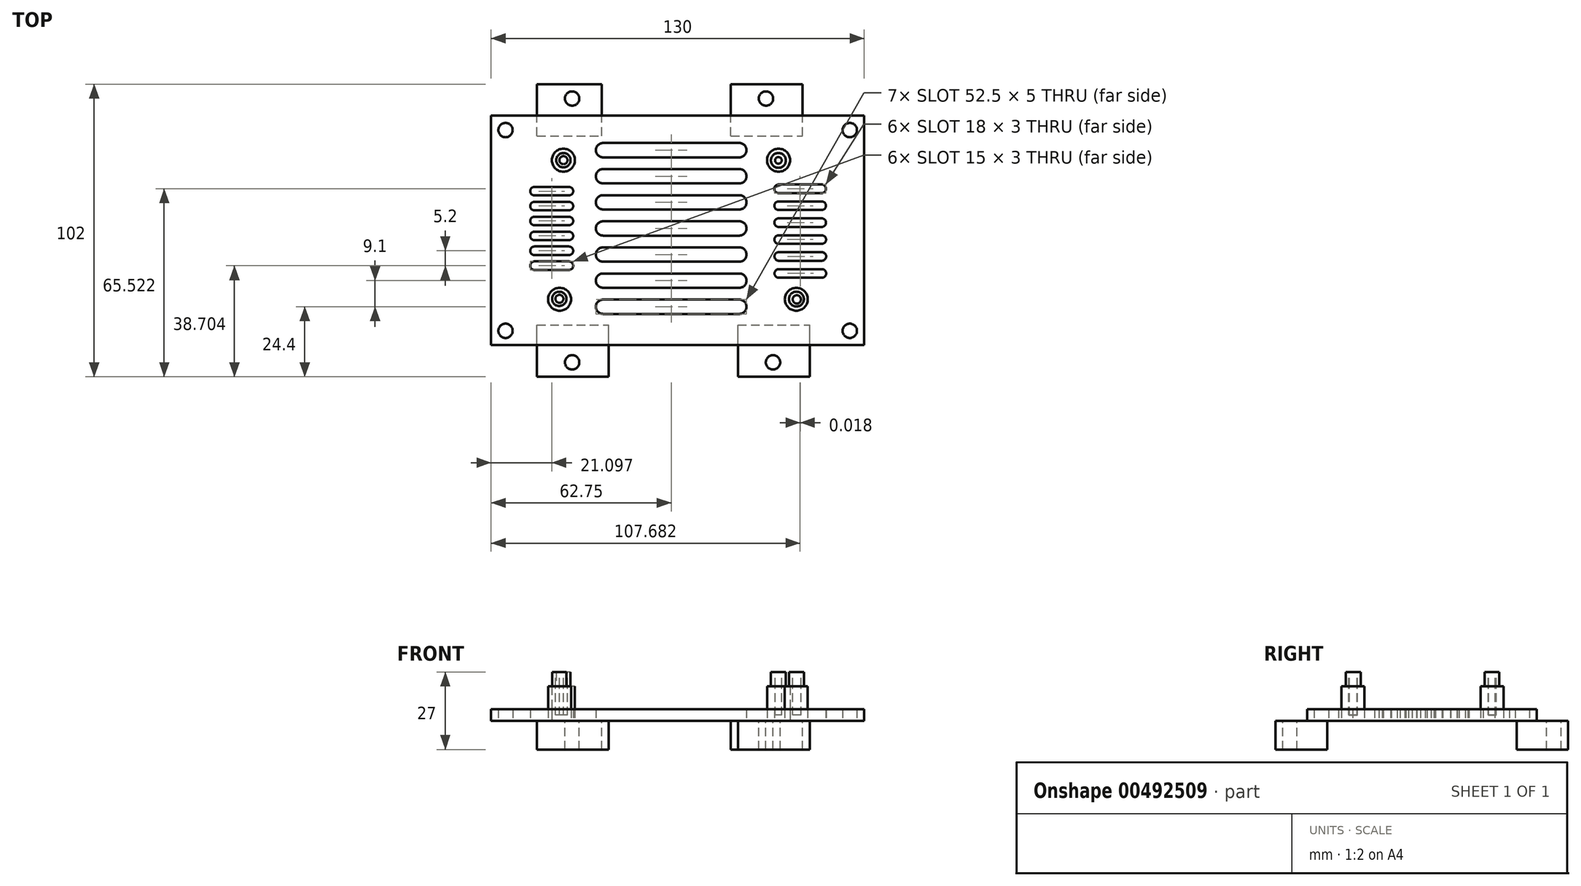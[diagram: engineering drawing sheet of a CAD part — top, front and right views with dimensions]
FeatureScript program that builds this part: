
annotation { "Feature Type Name" : "Feature", "Feature Type Description" : "" }
export const myFeature = defineFeature(function(context is Context, id is Id, definition is map)
    precondition{}
    {
        {
            var Q0;
            Q0=qCreatedBy(makeId("Top.planeOp"),FACE);
            var sketch = newSketch(context, id + "F0", { "sketchPlane" : qUnion([Q0])});
            skLineSegment(sketch, "E0.bottom", {"start": v(0, 0) * mm, "end": v(130, 0) * mm});
            skLineSegment(sketch, "E0.top", {"start": v(0, 80) * mm, "end": v(130, 80) * mm});
            skLineSegment(sketch, "E0.left", {"start": v(0, 0) * mm, "end": v(0, 80) * mm});
            skLineSegment(sketch, "E0.right", {"start": v(130, 0) * mm, "end": v(130, 80) * mm});
            skCircle(sketch, "E1", {"center": v(25.18, 64.5) * mm, "radius": 4 * mm});
            skCircle(sketch, "E2", {"center": v(23.85, 16) * mm, "radius": 4 * mm});
            skCircle(sketch, "E3", {"center": v(100.18, 64.5) * mm, "radius": 4 * mm});
            skCircle(sketch, "E4", {"center": v(106.35, 16) * mm, "radius": 4 * mm});
            skCircle(sketch, "E5", {"center": v(5, 75) * mm, "radius": 2.5 * mm});
            skCircle(sketch, "E6", {"center": v(5, 5) * mm, "radius": 2.5 * mm});
            skCircle(sketch, "E7", {"center": v(125, 75) * mm, "radius": 2.5 * mm});
            skCircle(sketch, "E8", {"center": v(125, 5) * mm, "radius": 2.5 * mm});
            skLineSegment(sketch, "E9.bottom", {"start": v(39, 70.5) * mm, "end": v(86.5, 70.5) * mm});
            skLineSegment(sketch, "E9.top", {"start": v(39, 65.5) * mm, "end": v(86.5, 65.5) * mm});
            skLineSegment(sketch, "E9.left", {"start": v(36.5, 68) * mm, "end": v(36.5, 68) * mm});
            skLineSegment(sketch, "E9.right", {"start": v(89, 68) * mm, "end": v(89, 68) * mm});
            skPoint(sketch, "E10.visualSharp", {"position": v(36.5, 70.5) * mm});
            skArc(sketch, "E10.filletArc", {"start": v(39, 70.5) * mm, "mid": v(37.23, 69.77) * mm, "end": v(36.5, 68) * mm});
            skPoint(sketch, "E11.visualSharp", {"position": v(36.5, 65.5) * mm});
            skArc(sketch, "E11.filletArc", {"start": v(36.5, 68) * mm, "mid": v(37.23, 66.23) * mm, "end": v(39, 65.5) * mm});
            skPoint(sketch, "E12.visualSharp", {"position": v(89, 70.5) * mm});
            skArc(sketch, "E12.filletArc", {"start": v(89, 68) * mm, "mid": v(88.27, 69.77) * mm, "end": v(86.5, 70.5) * mm});
            skPoint(sketch, "E13.visualSharp", {"position": v(89, 65.5) * mm});
            skArc(sketch, "E13.filletArc", {"start": v(86.5, 65.5) * mm, "mid": v(88.27, 66.23) * mm, "end": v(89, 68) * mm});
            skLineSegment(sketch, "E14.1.0.0", {"start": v(39, 56.4) * mm, "end": v(86.5, 56.4) * mm});
            skLineSegment(sketch, "E14.1.0.1", {"start": v(39, 61.4) * mm, "end": v(86.5, 61.4) * mm});
            skPoint(sketch, "E14.1.0.2", {"position": v(89, 56.4) * mm});
            skPoint(sketch, "E14.1.0.3", {"position": v(89, 61.4) * mm});
            skArc(sketch, "E14.1.0.4", {"start": v(39, 61.4) * mm, "mid": v(37.23, 60.67) * mm, "end": v(36.5, 58.9) * mm});
            skArc(sketch, "E14.1.0.5", {"start": v(86.5, 56.4) * mm, "mid": v(88.27, 57.13) * mm, "end": v(89, 58.9) * mm});
            skArc(sketch, "E14.1.0.6", {"start": v(36.5, 58.9) * mm, "mid": v(37.23, 57.13) * mm, "end": v(39, 56.4) * mm});
            skArc(sketch, "E14.1.0.7", {"start": v(89, 58.9) * mm, "mid": v(88.27, 60.67) * mm, "end": v(86.5, 61.4) * mm});
            skLineSegment(sketch, "E14.2.0.0", {"start": v(39, 47.3) * mm, "end": v(86.5, 47.3) * mm});
            skLineSegment(sketch, "E14.2.0.1", {"start": v(39, 52.3) * mm, "end": v(86.5, 52.3) * mm});
            skPoint(sketch, "E14.2.0.2", {"position": v(89, 47.3) * mm});
            skPoint(sketch, "E14.2.0.3", {"position": v(89, 52.3) * mm});
            skArc(sketch, "E14.2.0.4", {"start": v(39, 52.3) * mm, "mid": v(37.23, 51.57) * mm, "end": v(36.5, 49.8) * mm});
            skArc(sketch, "E14.2.0.5", {"start": v(86.5, 47.3) * mm, "mid": v(88.27, 48.03) * mm, "end": v(89, 49.8) * mm});
            skArc(sketch, "E14.2.0.6", {"start": v(36.5, 49.8) * mm, "mid": v(37.23, 48.03) * mm, "end": v(39, 47.3) * mm});
            skArc(sketch, "E14.2.0.7", {"start": v(89, 49.8) * mm, "mid": v(88.27, 51.57) * mm, "end": v(86.5, 52.3) * mm});
            skLineSegment(sketch, "E14.3.0.0", {"start": v(39, 38.2) * mm, "end": v(86.5, 38.2) * mm});
            skLineSegment(sketch, "E14.3.0.1", {"start": v(39, 43.2) * mm, "end": v(86.5, 43.2) * mm});
            skPoint(sketch, "E14.3.0.2", {"position": v(89, 38.2) * mm});
            skPoint(sketch, "E14.3.0.3", {"position": v(89, 43.2) * mm});
            skArc(sketch, "E14.3.0.4", {"start": v(39, 43.2) * mm, "mid": v(37.23, 42.47) * mm, "end": v(36.5, 40.7) * mm});
            skArc(sketch, "E14.3.0.5", {"start": v(86.5, 38.2) * mm, "mid": v(88.27, 38.93) * mm, "end": v(89, 40.7) * mm});
            skArc(sketch, "E14.3.0.6", {"start": v(36.5, 40.7) * mm, "mid": v(37.23, 38.93) * mm, "end": v(39, 38.2) * mm});
            skArc(sketch, "E14.3.0.7", {"start": v(89, 40.7) * mm, "mid": v(88.27, 42.47) * mm, "end": v(86.5, 43.2) * mm});
            skLineSegment(sketch, "E14.4.0.0", {"start": v(39, 29.1) * mm, "end": v(86.5, 29.1) * mm});
            skLineSegment(sketch, "E14.4.0.1", {"start": v(39, 34.1) * mm, "end": v(86.5, 34.1) * mm});
            skPoint(sketch, "E14.4.0.2", {"position": v(89, 29.1) * mm});
            skPoint(sketch, "E14.4.0.3", {"position": v(89, 34.1) * mm});
            skArc(sketch, "E14.4.0.4", {"start": v(39, 34.1) * mm, "mid": v(37.23, 33.37) * mm, "end": v(36.5, 31.6) * mm});
            skArc(sketch, "E14.4.0.5", {"start": v(86.5, 29.1) * mm, "mid": v(88.27, 29.83) * mm, "end": v(89, 31.6) * mm});
            skArc(sketch, "E14.4.0.6", {"start": v(36.5, 31.6) * mm, "mid": v(37.23, 29.83) * mm, "end": v(39, 29.1) * mm});
            skArc(sketch, "E14.4.0.7", {"start": v(89, 31.6) * mm, "mid": v(88.27, 33.37) * mm, "end": v(86.5, 34.1) * mm});
            skLineSegment(sketch, "E14.5.0.0", {"start": v(39, 20) * mm, "end": v(86.5, 20) * mm});
            skLineSegment(sketch, "E14.5.0.1", {"start": v(39, 25) * mm, "end": v(86.5, 25) * mm});
            skPoint(sketch, "E14.5.0.2", {"position": v(89, 20) * mm});
            skPoint(sketch, "E14.5.0.3", {"position": v(89, 25) * mm});
            skArc(sketch, "E14.5.0.4", {"start": v(39, 25) * mm, "mid": v(37.23, 24.27) * mm, "end": v(36.5, 22.5) * mm});
            skArc(sketch, "E14.5.0.5", {"start": v(86.5, 20) * mm, "mid": v(88.27, 20.73) * mm, "end": v(89, 22.5) * mm});
            skArc(sketch, "E14.5.0.6", {"start": v(36.5, 22.5) * mm, "mid": v(37.23, 20.73) * mm, "end": v(39, 20) * mm});
            skArc(sketch, "E14.5.0.7", {"start": v(89, 22.5) * mm, "mid": v(88.27, 24.27) * mm, "end": v(86.5, 25) * mm});
            skLineSegment(sketch, "E14.6.0.0", {"start": v(39, 10.9) * mm, "end": v(86.5, 10.9) * mm});
            skLineSegment(sketch, "E14.6.0.1", {"start": v(39, 15.9) * mm, "end": v(86.5, 15.9) * mm});
            skPoint(sketch, "E14.6.0.2", {"position": v(89, 10.9) * mm});
            skPoint(sketch, "E14.6.0.3", {"position": v(89, 15.9) * mm});
            skArc(sketch, "E14.6.0.4", {"start": v(39, 15.9) * mm, "mid": v(37.23, 15.17) * mm, "end": v(36.5, 13.4) * mm});
            skArc(sketch, "E14.6.0.5", {"start": v(86.5, 10.9) * mm, "mid": v(88.27, 11.63) * mm, "end": v(89, 13.4) * mm});
            skArc(sketch, "E14.6.0.6", {"start": v(36.5, 13.4) * mm, "mid": v(37.23, 11.63) * mm, "end": v(39, 10.9) * mm});
            skArc(sketch, "E14.6.0.7", {"start": v(89, 13.4) * mm, "mid": v(88.27, 15.17) * mm, "end": v(86.5, 15.9) * mm});
            skLineSegment(sketch, "E14.direction1", {"start": v(39, 65.5) * mm, "end": v(39, 56.4) * mm, "construction": true});
            skLineSegment(sketch, "E15.bottom", {"start": v(100.18, 56.02) * mm, "end": v(115.18, 56.02) * mm});
            skLineSegment(sketch, "E15.top", {"start": v(100.18, 53.02) * mm, "end": v(115.18, 53.02) * mm});
            skLineSegment(sketch, "E15.left", {"start": v(98.68, 54.52) * mm, "end": v(98.68, 54.52) * mm});
            skLineSegment(sketch, "E15.right", {"start": v(116.68, 54.52) * mm, "end": v(116.68, 54.52) * mm});
            skPoint(sketch, "E16.visualSharp", {"position": v(98.68, 56.02) * mm});
            skArc(sketch, "E16.filletArc", {"start": v(100.18, 56.02) * mm, "mid": v(99.12, 55.58) * mm, "end": v(98.68, 54.52) * mm});
            skPoint(sketch, "E17.visualSharp", {"position": v(98.68, 53.02) * mm});
            skArc(sketch, "E17.filletArc", {"start": v(98.68, 54.52) * mm, "mid": v(99.12, 53.46) * mm, "end": v(100.18, 53.02) * mm});
            skPoint(sketch, "E18.visualSharp", {"position": v(116.68, 56.02) * mm});
            skArc(sketch, "E18.filletArc", {"start": v(116.68, 54.52) * mm, "mid": v(116.24, 55.58) * mm, "end": v(115.18, 56.02) * mm});
            skPoint(sketch, "E19.visualSharp", {"position": v(116.68, 53.02) * mm});
            skArc(sketch, "E19.filletArc", {"start": v(115.18, 53.02) * mm, "mid": v(116.24, 53.46) * mm, "end": v(116.68, 54.52) * mm});
            skPoint(sketch, "E20.1.0.0", {"position": v(116.7, 50.12) * mm});
            skPoint(sketch, "E20.1.0.1", {"position": v(98.7, 50.12) * mm});
            skPoint(sketch, "E20.1.0.2", {"position": v(98.7, 47.12) * mm});
            skLineSegment(sketch, "E20.1.0.3", {"start": v(100.2, 50.12) * mm, "end": v(115.2, 50.12) * mm});
            skLineSegment(sketch, "E20.1.0.4", {"start": v(100.2, 47.12) * mm, "end": v(115.2, 47.12) * mm});
            skPoint(sketch, "E20.1.0.5", {"position": v(116.7, 47.12) * mm});
            skArc(sketch, "E20.1.0.6", {"start": v(100.2, 50.12) * mm, "mid": v(99.14, 49.68) * mm, "end": v(98.7, 48.62) * mm});
            skArc(sketch, "E20.1.0.7", {"start": v(115.2, 47.12) * mm, "mid": v(116.26, 47.56) * mm, "end": v(116.7, 48.62) * mm});
            skArc(sketch, "E20.1.0.8", {"start": v(116.7, 48.62) * mm, "mid": v(116.26, 49.68) * mm, "end": v(115.2, 50.12) * mm});
            skArc(sketch, "E20.1.0.9", {"start": v(98.7, 48.62) * mm, "mid": v(99.14, 47.56) * mm, "end": v(100.2, 47.12) * mm});
            skPoint(sketch, "E20.2.0.0", {"position": v(116.72, 44.22) * mm});
            skPoint(sketch, "E20.2.0.1", {"position": v(98.72, 44.22) * mm});
            skPoint(sketch, "E20.2.0.2", {"position": v(98.72, 41.22) * mm});
            skLineSegment(sketch, "E20.2.0.3", {"start": v(100.22, 44.22) * mm, "end": v(115.22, 44.22) * mm});
            skLineSegment(sketch, "E20.2.0.4", {"start": v(100.22, 41.22) * mm, "end": v(115.22, 41.22) * mm});
            skPoint(sketch, "E20.2.0.5", {"position": v(116.72, 41.22) * mm});
            skArc(sketch, "E20.2.0.6", {"start": v(100.22, 44.22) * mm, "mid": v(99.16, 43.78) * mm, "end": v(98.72, 42.72) * mm});
            skArc(sketch, "E20.2.0.7", {"start": v(115.22, 41.22) * mm, "mid": v(116.28, 41.66) * mm, "end": v(116.72, 42.72) * mm});
            skArc(sketch, "E20.2.0.8", {"start": v(116.72, 42.72) * mm, "mid": v(116.28, 43.78) * mm, "end": v(115.22, 44.22) * mm});
            skArc(sketch, "E20.2.0.9", {"start": v(98.72, 42.72) * mm, "mid": v(99.16, 41.66) * mm, "end": v(100.22, 41.22) * mm});
            skPoint(sketch, "E20.3.0.0", {"position": v(116.74, 38.32) * mm});
            skPoint(sketch, "E20.3.0.1", {"position": v(98.74, 38.32) * mm});
            skPoint(sketch, "E20.3.0.2", {"position": v(98.74, 35.32) * mm});
            skLineSegment(sketch, "E20.3.0.3", {"start": v(100.24, 38.32) * mm, "end": v(115.24, 38.32) * mm});
            skLineSegment(sketch, "E20.3.0.4", {"start": v(100.24, 35.32) * mm, "end": v(115.24, 35.32) * mm});
            skPoint(sketch, "E20.3.0.5", {"position": v(116.74, 35.32) * mm});
            skArc(sketch, "E20.3.0.6", {"start": v(100.24, 38.32) * mm, "mid": v(99.18, 37.88) * mm, "end": v(98.74, 36.82) * mm});
            skArc(sketch, "E20.3.0.7", {"start": v(115.24, 35.32) * mm, "mid": v(116.3, 35.76) * mm, "end": v(116.74, 36.82) * mm});
            skArc(sketch, "E20.3.0.8", {"start": v(116.74, 36.82) * mm, "mid": v(116.3, 37.88) * mm, "end": v(115.24, 38.32) * mm});
            skArc(sketch, "E20.3.0.9", {"start": v(98.74, 36.82) * mm, "mid": v(99.18, 35.76) * mm, "end": v(100.24, 35.32) * mm});
            skPoint(sketch, "E20.4.0.0", {"position": v(116.75, 32.42) * mm});
            skPoint(sketch, "E20.4.0.1", {"position": v(98.75, 32.42) * mm});
            skPoint(sketch, "E20.4.0.2", {"position": v(98.75, 29.42) * mm});
            skLineSegment(sketch, "E20.4.0.3", {"start": v(100.25, 32.42) * mm, "end": v(115.25, 32.42) * mm});
            skLineSegment(sketch, "E20.4.0.4", {"start": v(100.25, 29.42) * mm, "end": v(115.25, 29.42) * mm});
            skPoint(sketch, "E20.4.0.5", {"position": v(116.75, 29.42) * mm});
            skArc(sketch, "E20.4.0.6", {"start": v(100.25, 32.42) * mm, "mid": v(99.2, 31.98) * mm, "end": v(98.75, 30.92) * mm});
            skArc(sketch, "E20.4.0.7", {"start": v(115.25, 29.42) * mm, "mid": v(116.32, 29.86) * mm, "end": v(116.75, 30.92) * mm});
            skArc(sketch, "E20.4.0.8", {"start": v(116.75, 30.92) * mm, "mid": v(116.32, 31.98) * mm, "end": v(115.25, 32.42) * mm});
            skArc(sketch, "E20.4.0.9", {"start": v(98.75, 30.92) * mm, "mid": v(99.2, 29.86) * mm, "end": v(100.25, 29.42) * mm});
            skPoint(sketch, "E20.5.0.0", {"position": v(116.77, 26.52) * mm});
            skPoint(sketch, "E20.5.0.1", {"position": v(98.77, 26.52) * mm});
            skPoint(sketch, "E20.5.0.2", {"position": v(98.77, 23.52) * mm});
            skLineSegment(sketch, "E20.5.0.3", {"start": v(100.27, 26.52) * mm, "end": v(115.27, 26.52) * mm});
            skLineSegment(sketch, "E20.5.0.4", {"start": v(100.27, 23.52) * mm, "end": v(115.27, 23.52) * mm});
            skPoint(sketch, "E20.5.0.5", {"position": v(116.77, 23.52) * mm});
            skArc(sketch, "E20.5.0.6", {"start": v(100.27, 26.52) * mm, "mid": v(99.21, 26.08) * mm, "end": v(98.77, 25.02) * mm});
            skArc(sketch, "E20.5.0.7", {"start": v(115.27, 23.52) * mm, "mid": v(116.33, 23.96) * mm, "end": v(116.77, 25.02) * mm});
            skArc(sketch, "E20.5.0.8", {"start": v(116.77, 25.02) * mm, "mid": v(116.33, 26.08) * mm, "end": v(115.27, 26.52) * mm});
            skArc(sketch, "E20.5.0.9", {"start": v(98.77, 25.02) * mm, "mid": v(99.21, 23.96) * mm, "end": v(100.27, 23.52) * mm});
            skLineSegment(sketch, "E20.direction1", {"start": v(98.68, 53.02) * mm, "end": v(98.7, 47.12) * mm, "construction": true});
            skLineSegment(sketch, "E21.bottom", {"start": v(15.1, 55.2) * mm, "end": v(27.1, 55.2) * mm});
            skLineSegment(sketch, "E21.top", {"start": v(15.1, 52.2) * mm, "end": v(27.1, 52.2) * mm});
            skLineSegment(sketch, "E21.left", {"start": v(13.6, 53.7) * mm, "end": v(13.6, 53.7) * mm});
            skLineSegment(sketch, "E21.right", {"start": v(28.6, 53.7) * mm, "end": v(28.6, 53.7) * mm});
            skPoint(sketch, "E22.visualSharp", {"position": v(13.6, 55.2) * mm});
            skArc(sketch, "E22.filletArc", {"start": v(15.1, 55.2) * mm, "mid": v(14.04, 54.76) * mm, "end": v(13.6, 53.7) * mm});
            skPoint(sketch, "E23.visualSharp", {"position": v(13.6, 52.2) * mm});
            skArc(sketch, "E23.filletArc", {"start": v(13.6, 53.7) * mm, "mid": v(14.04, 52.64) * mm, "end": v(15.1, 52.2) * mm});
            skPoint(sketch, "E24.visualSharp", {"position": v(28.6, 55.2) * mm});
            skArc(sketch, "E24.filletArc", {"start": v(28.6, 53.7) * mm, "mid": v(28.16, 54.76) * mm, "end": v(27.1, 55.2) * mm});
            skPoint(sketch, "E25.visualSharp", {"position": v(28.6, 52.2) * mm});
            skArc(sketch, "E25.filletArc", {"start": v(27.1, 52.2) * mm, "mid": v(28.16, 52.64) * mm, "end": v(28.6, 53.7) * mm});
            skPoint(sketch, "E26.1.0.0", {"position": v(13.6, 50) * mm});
            skLineSegment(sketch, "E26.1.0.1", {"start": v(15.1, 50) * mm, "end": v(27.1, 50) * mm});
            skArc(sketch, "E26.1.0.2", {"start": v(28.6, 48.5) * mm, "mid": v(28.16, 49.56) * mm, "end": v(27.1, 50) * mm});
            skPoint(sketch, "E26.1.0.3", {"position": v(28.6, 47) * mm});
            skArc(sketch, "E26.1.0.4", {"start": v(13.6, 48.5) * mm, "mid": v(14.04, 47.44) * mm, "end": v(15.1, 47) * mm});
            skArc(sketch, "E26.1.0.5", {"start": v(27.1, 47) * mm, "mid": v(28.16, 47.44) * mm, "end": v(28.6, 48.5) * mm});
            skArc(sketch, "E26.1.0.6", {"start": v(15.1, 50) * mm, "mid": v(14.04, 49.56) * mm, "end": v(13.6, 48.5) * mm});
            skPoint(sketch, "E26.1.0.7", {"position": v(28.6, 50) * mm});
            skPoint(sketch, "E26.1.0.8", {"position": v(13.6, 47) * mm});
            skLineSegment(sketch, "E26.1.0.9", {"start": v(15.1, 47) * mm, "end": v(27.1, 47) * mm});
            skPoint(sketch, "E26.2.0.0", {"position": v(13.6, 44.8) * mm});
            skLineSegment(sketch, "E26.2.0.1", {"start": v(15.1, 44.8) * mm, "end": v(27.1, 44.8) * mm});
            skArc(sketch, "E26.2.0.2", {"start": v(28.6, 43.3) * mm, "mid": v(28.16, 44.36) * mm, "end": v(27.1, 44.8) * mm});
            skPoint(sketch, "E26.2.0.3", {"position": v(28.6, 41.8) * mm});
            skArc(sketch, "E26.2.0.4", {"start": v(13.6, 43.3) * mm, "mid": v(14.04, 42.24) * mm, "end": v(15.1, 41.8) * mm});
            skArc(sketch, "E26.2.0.5", {"start": v(27.1, 41.8) * mm, "mid": v(28.16, 42.24) * mm, "end": v(28.6, 43.3) * mm});
            skArc(sketch, "E26.2.0.6", {"start": v(15.1, 44.8) * mm, "mid": v(14.04, 44.36) * mm, "end": v(13.6, 43.3) * mm});
            skPoint(sketch, "E26.2.0.7", {"position": v(28.6, 44.8) * mm});
            skPoint(sketch, "E26.2.0.8", {"position": v(13.6, 41.8) * mm});
            skLineSegment(sketch, "E26.2.0.9", {"start": v(15.1, 41.8) * mm, "end": v(27.1, 41.8) * mm});
            skPoint(sketch, "E26.3.0.0", {"position": v(13.6, 39.6) * mm});
            skLineSegment(sketch, "E26.3.0.1", {"start": v(15.1, 39.6) * mm, "end": v(27.1, 39.6) * mm});
            skArc(sketch, "E26.3.0.2", {"start": v(28.6, 38.1) * mm, "mid": v(28.16, 39.16) * mm, "end": v(27.1, 39.6) * mm});
            skPoint(sketch, "E26.3.0.3", {"position": v(28.6, 36.6) * mm});
            skArc(sketch, "E26.3.0.4", {"start": v(13.6, 38.1) * mm, "mid": v(14.04, 37.04) * mm, "end": v(15.1, 36.6) * mm});
            skArc(sketch, "E26.3.0.5", {"start": v(27.1, 36.6) * mm, "mid": v(28.16, 37.04) * mm, "end": v(28.6, 38.1) * mm});
            skArc(sketch, "E26.3.0.6", {"start": v(15.1, 39.6) * mm, "mid": v(14.04, 39.16) * mm, "end": v(13.6, 38.1) * mm});
            skPoint(sketch, "E26.3.0.7", {"position": v(28.6, 39.6) * mm});
            skPoint(sketch, "E26.3.0.8", {"position": v(13.6, 36.6) * mm});
            skLineSegment(sketch, "E26.3.0.9", {"start": v(15.1, 36.6) * mm, "end": v(27.1, 36.6) * mm});
            skPoint(sketch, "E26.4.0.0", {"position": v(13.6, 34.4) * mm});
            skLineSegment(sketch, "E26.4.0.1", {"start": v(15.1, 34.4) * mm, "end": v(27.1, 34.4) * mm});
            skArc(sketch, "E26.4.0.2", {"start": v(28.6, 32.9) * mm, "mid": v(28.16, 33.96) * mm, "end": v(27.1, 34.4) * mm});
            skPoint(sketch, "E26.4.0.3", {"position": v(28.6, 31.4) * mm});
            skArc(sketch, "E26.4.0.4", {"start": v(13.6, 32.9) * mm, "mid": v(14.04, 31.84) * mm, "end": v(15.1, 31.4) * mm});
            skArc(sketch, "E26.4.0.5", {"start": v(27.1, 31.4) * mm, "mid": v(28.16, 31.84) * mm, "end": v(28.6, 32.9) * mm});
            skArc(sketch, "E26.4.0.6", {"start": v(15.1, 34.4) * mm, "mid": v(14.04, 33.96) * mm, "end": v(13.6, 32.9) * mm});
            skPoint(sketch, "E26.4.0.7", {"position": v(28.6, 34.4) * mm});
            skPoint(sketch, "E26.4.0.8", {"position": v(13.6, 31.4) * mm});
            skLineSegment(sketch, "E26.4.0.9", {"start": v(15.1, 31.4) * mm, "end": v(27.1, 31.4) * mm});
            skPoint(sketch, "E26.5.0.0", {"position": v(13.6, 29.2) * mm});
            skLineSegment(sketch, "E26.5.0.1", {"start": v(15.1, 29.2) * mm, "end": v(27.1, 29.2) * mm});
            skArc(sketch, "E26.5.0.2", {"start": v(28.6, 27.7) * mm, "mid": v(28.16, 28.76) * mm, "end": v(27.1, 29.2) * mm});
            skPoint(sketch, "E26.5.0.3", {"position": v(28.6, 26.2) * mm});
            skArc(sketch, "E26.5.0.4", {"start": v(13.6, 27.7) * mm, "mid": v(14.04, 26.64) * mm, "end": v(15.1, 26.2) * mm});
            skArc(sketch, "E26.5.0.5", {"start": v(27.1, 26.2) * mm, "mid": v(28.16, 26.64) * mm, "end": v(28.6, 27.7) * mm});
            skArc(sketch, "E26.5.0.6", {"start": v(15.1, 29.2) * mm, "mid": v(14.04, 28.76) * mm, "end": v(13.6, 27.7) * mm});
            skPoint(sketch, "E26.5.0.7", {"position": v(28.6, 29.2) * mm});
            skPoint(sketch, "E26.5.0.8", {"position": v(13.6, 26.2) * mm});
            skLineSegment(sketch, "E26.5.0.9", {"start": v(15.1, 26.2) * mm, "end": v(27.1, 26.2) * mm});
            skLineSegment(sketch, "E26.direction1", {"start": v(13.6, 52.2) * mm, "end": v(13.6, 47) * mm, "construction": true});
            skSolve(sketch);
        }
        {
            var Q0;
            Q0=makeQuery(id+"F0.imprint","IMPRINT",FACE,{"disambiguationData":[TD([[makeQuery(id+"F0.imprint","IMPRINT",EDGE,{"derivedFrom":sQuery(id+"F0.wireOp",EDGE,"E1")}),1.0]])]});
            var Q1;
            Q1=makeQuery(id+"F0.imprint","IMPRINT",FACE,{"disambiguationData":[TD([[makeQuery(id+"F0.imprint","IMPRINT",EDGE,{"derivedFrom":sQuery(id+"F0.wireOp",EDGE,"E3")}),1.0]])]});
            var Q2;
            Q2=makeQuery(id+"F0.imprint","IMPRINT",FACE,{"disambiguationData":[TD([[makeQuery(id+"F0.imprint","IMPRINT",EDGE,{"derivedFrom":sQuery(id+"F0.wireOp",EDGE,"E4")}),1.0]])]});
            var Q3;
            Q3=makeQuery(id+"F0.imprint","IMPRINT",FACE,{"disambiguationData":[TD([[makeQuery(id+"F0.imprint","IMPRINT",EDGE,{"derivedFrom":sQuery(id+"F0.wireOp",EDGE,"E2")}),1.0]])]});
            extrude(context, id + "F1", {"entities" : qUnion([Q0, Q1, Q2, Q3]), "depth" : 12 * mm});
        }
        {
            var Q0;
            Q0=makeQuery(id+"F1.opExtrude","CAP_FACE",FACE,{"disambiguationData":[OSD([sQuery(id+"F0.wireOp",EDGE,"E1")])],"isStart":false});
            var sketch = newSketch(context, id + "F2", { "sketchPlane" : qUnion([Q0])});
            skCircle(sketch, "E27", {"center": v(25.18, 64.5) * mm, "radius": 2.5 * mm});
            skCircle(sketch, "E28", {"center": v(23.73, 16.15) * mm, "radius": 2.5 * mm});
            skCircle(sketch, "E29", {"center": v(100.12, 64.42) * mm, "radius": 2.6 * mm});
            skCircle(sketch, "E30", {"center": v(106.4, 16.06) * mm, "radius": 2.6 * mm});
            skSolve(sketch);
        }
        {
            var Q0;
            Q0=makeQuery(id+"F2.imprint","IMPRINT",FACE,{"disambiguationData":[TD([[makeQuery(id+"F2.imprint","IMPRINT",EDGE,{"derivedFrom":sQuery(id+"F2.wireOp",EDGE,"E27")}),1.0]])]});
            var Q1;
            Q1=makeQuery(id+"F2.imprint","IMPRINT",FACE,{"disambiguationData":[TD([[makeQuery(id+"F2.imprint","IMPRINT",EDGE,{"derivedFrom":sQuery(id+"F2.wireOp",EDGE,"E28")}),1.0]])]});
            var Q2;
            Q2=makeQuery(id+"F2.imprint","IMPRINT",FACE,{"disambiguationData":[TD([[makeQuery(id+"F2.imprint","IMPRINT",EDGE,{"derivedFrom":sQuery(id+"F2.wireOp",EDGE,"E29")}),1.0]])]});
            var Q3;
            Q3=makeQuery(id+"F2.imprint","IMPRINT",FACE,{"disambiguationData":[TD([[makeQuery(id+"F2.imprint","IMPRINT",EDGE,{"derivedFrom":sQuery(id+"F2.wireOp",EDGE,"E30")}),1.0]])]});
            extrude(context, id + "F3", {"entities" : qUnion([Q0, Q1, Q2, Q3]), "flatOperationType" : FlatOperationType.REMOVE, "offsetDistance" : 25 * mm, "depth" : 5 * mm, "domain" : OperationDomain.MODEL});
        }
        {
            var Q0;
            Q0=makeQuery(id+"F0.imprint","IMPRINT",FACE,{"disambiguationData":[TD([[makeQuery(id+"F0.imprint","IMPRINT",EDGE,{"derivedFrom":sQuery(id+"F0.wireOp",EDGE,"E0.bottom")}),1.0]])]});
            extrude(context, id + "F4", {"entities" : qUnion([Q0]), "depth" : 4 * mm});
        }
        {
            var Q0;
            Q0=makeQuery(id+"F3.opExtrude","CAP_FACE",FACE,{"disambiguationData":[OSD([sQuery(id+"F2.wireOp",EDGE,"E27")])],"isStart":false});
            var sketch = newSketch(context, id + "F5", { "sketchPlane" : qUnion([Q0])});
            skCircle(sketch, "E31", {"center": v(25.18, 64.5) * mm, "radius": 1.4 * mm});
            skCircle(sketch, "E32", {"center": v(23.8, 16.16) * mm, "radius": 1.39 * mm});
            skCircle(sketch, "E33", {"center": v(100.1, 64.44) * mm, "radius": 1.16 * mm});
            skCircle(sketch, "E34", {"center": v(106.55, 15.96) * mm, "radius": 1.44 * mm});
            skSolve(sketch);
        }
        {
            var Q0;
            Q0=makeQuery(id+"F5.imprint","IMPRINT",FACE,{"disambiguationData":[TD([[makeQuery(id+"F5.imprint","IMPRINT",EDGE,{"derivedFrom":sQuery(id+"F5.wireOp",EDGE,"E32")}),1.0]])]});
            extrude(context, id + "F6", {"entities" : qUnion([Q0]), "operationType" : NewBodyOperationType.REMOVE, "oppositeDirection" : true, "depth" : 15 * mm});
        }
        {
            var Q0;
            Q0=makeQuery(id+"F5.imprint","IMPRINT",FACE,{"disambiguationData":[TD([[makeQuery(id+"F5.imprint","IMPRINT",EDGE,{"derivedFrom":sQuery(id+"F5.wireOp",EDGE,"E31")}),1.0]])]});
            extrude(context, id + "F7", {"entities" : qUnion([Q0]), "operationType" : NewBodyOperationType.REMOVE, "oppositeDirection" : true, "depth" : 15 * mm});
        }
        {
            var Q0;
            Q0=makeQuery(id+"F5.imprint","IMPRINT",FACE,{"disambiguationData":[TD([[makeQuery(id+"F5.imprint","IMPRINT",EDGE,{"derivedFrom":sQuery(id+"F5.wireOp",EDGE,"E33")}),1.0]])]});
            extrude(context, id + "F8", {"entities" : qUnion([Q0]), "operationType" : NewBodyOperationType.REMOVE, "oppositeDirection" : true, "depth" : 15 * mm});
        }
        {
            var Q0;
            Q0=makeQuery(id+"F5.imprint","IMPRINT",FACE,{"disambiguationData":[TD([[makeQuery(id+"F5.imprint","IMPRINT",EDGE,{"derivedFrom":sQuery(id+"F5.wireOp",EDGE,"E34")}),1.0]])]});
            extrude(context, id + "F9", {"entities" : qUnion([Q0]), "operationType" : NewBodyOperationType.REMOVE, "oppositeDirection" : true, "depth" : 15 * mm});
        }
        {
            var Q0;
            Q0=makeQuery(id+"F0.imprint","IMPRINT",FACE,{"disambiguationData":[TD([[makeQuery(id+"F0.imprint","IMPRINT",EDGE,{"derivedFrom":sQuery(id+"F0.wireOp",EDGE,"E0.bottom")}),1.0]])]});
            var sketch = newSketch(context, id + "F10", { "sketchPlane" : qUnion([Q0])});
            skLineSegment(sketch, "E35.bottom", {"start": v(16, -11) * mm, "end": v(41, -11) * mm});
            skLineSegment(sketch, "E35.top", {"start": v(16, 7) * mm, "end": v(41, 7) * mm});
            skLineSegment(sketch, "E35.left", {"start": v(16, -11) * mm, "end": v(16, 7) * mm});
            skLineSegment(sketch, "E35.right", {"start": v(41, -11) * mm, "end": v(41, 7) * mm});
            skLineSegment(sketch, "E36.bottom", {"start": v(86, -11) * mm, "end": v(111, -11) * mm});
            skLineSegment(sketch, "E36.top", {"start": v(86, 7) * mm, "end": v(111, 7) * mm});
            skLineSegment(sketch, "E36.left", {"start": v(86, -11) * mm, "end": v(86, 7) * mm});
            skLineSegment(sketch, "E36.right", {"start": v(111, -11) * mm, "end": v(111, 7) * mm});
            skLineSegment(sketch, "E37.bottom", {"start": v(16, 73) * mm, "end": v(38.56, 73) * mm});
            skLineSegment(sketch, "E37.top", {"start": v(16, 91) * mm, "end": v(38.56, 91) * mm});
            skLineSegment(sketch, "E37.left", {"start": v(16, 73) * mm, "end": v(16, 91) * mm});
            skLineSegment(sketch, "E37.right", {"start": v(38.56, 73) * mm, "end": v(38.56, 91) * mm});
            skLineSegment(sketch, "E38.bottom", {"start": v(83.56, 73) * mm, "end": v(108.56, 73) * mm});
            skLineSegment(sketch, "E38.top", {"start": v(83.56, 91) * mm, "end": v(108.56, 91) * mm});
            skLineSegment(sketch, "E38.left", {"start": v(83.56, 73) * mm, "end": v(83.56, 91) * mm});
            skLineSegment(sketch, "E38.right", {"start": v(108.56, 73) * mm, "end": v(108.56, 91) * mm});
            skCircle(sketch, "E39", {"center": v(28.23, -6) * mm, "radius": 2.5 * mm});
            skCircle(sketch, "E40", {"center": v(98.23, -6) * mm, "radius": 2.5 * mm});
            skCircle(sketch, "E41", {"center": v(95.8, 86) * mm, "radius": 2.5 * mm});
            skCircle(sketch, "E42", {"center": v(28.23, 86) * mm, "radius": 2.5 * mm});
            skSolve(sketch);
        }
        {
            var Q0;
            Q0 = qSketchRegion(id + "F10", true);
            extrude(context, id + "F11", {"entities" : qUnion([Q0]), "operationType" : NewBodyOperationType.ADD, "oppositeDirection" : true, "depth" : 10 * mm});
        }
    });
